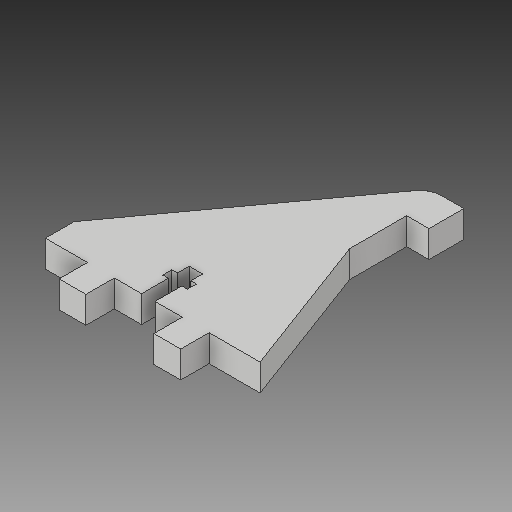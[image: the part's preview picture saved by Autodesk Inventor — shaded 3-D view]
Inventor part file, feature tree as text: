
AUTODESK INVENTOR PART (.ipt)
format: ipt  version: 2018 (Build 220112000, 112)  size: 131,584 bytes
history: native  units: mm
features: extrude x1, sketch x1
ambient origin geometry x8: Origin, YZ Plane, XZ Plane, XY Plane, X Axis, Y Axis, Z Axis, Center Point
bodies: Solid1 (feature_tree)
feature tree (2):
  extrude  "Extrusion1"  [1 undecoded]
  sketch  "Sketch1"  dims[d0=6.0mm d1=0.0mm]
note: 1 required parameter value undecoded (feature->parameter linkage not recoverable at this tier; creation-order binding heuristic only, values carry confidence <= 0.55)
